# Revit family: Kingsway Sentry Doorset - S_Duralux 405 x 405mm
name_source: partatom
category: Doors
revit_build: Autodesk Revit 2017 (Build: 20160225_1515(x64)
units: mm (PartAtom-declared; Revit-internal decimal feet)

## family parameters
Always vertical = Yes
Cut with Voids When Loaded = No
Host = Wall
OmniClass Number = 23.30.10.00
OmniClass Title = Doors
Room Calculation Point = No
Shared = No

## types (1)
- 1010 x 2100
    Action = Double (Anti-Barricade)
    Analytic Construction = <None>
    Architrave Material = Solid hardwood.
    Bead Material = Stainless steel.
    Configuration = Single Leaf
    Description = In the event of a barricade the SENTRY mechanism
unlocks and folds to allow the door to swing outwards. Equipped with ligature sensors around the three door edges.
    Door - Leaf Finish Notes = Classic Veneer – 'Oak', 'Ash', or 'Beech'
Classic Laminate – 'Formica Door Collection Matte58 Woods', or 'Formica Collection Colors'
Signature - 'Malmo (Egger H877 ST86 Light Lakeland Acacia)', 'Manhattan (Egger H1734 ST9 Intarsie Walnut Horizontal)', or 'Mayfair (Egger H853 ST86 Lava Grey Fleetwood Horizontal)'
    Door Leaf Height = 2054 mm  [stored 6.73885 ft]
    Door Leaf Width = 844 mm
    Durability = Severe Duty Mechanical Strength (DD171).
    Error = No
    Fire Rating = NFR / FD30S
    Frame Thickness = 32 mm  [stored 0.104987 ft]
    Frame Thickness Leading Edge = 44 mm
    Function = Interior
    Height = 2100 mm
    KG280FoldingAntiBarricadeHinge = Yes
    Keynote = L20
    Leaf Core Structure = Flamebreak - Solid timber core comprising three layers of solid hardwood.
    Leaf Height Limits = 2100 mm
    Leaf Swing Radius = 889 mm
    Leaf Width Limits = 1100 mm
    Lipping Material = Exposed 10mm solid hardwood to all four edges.
    Manufacturer = Kingsway Group
    Model = Sentry Doorset
    Rough Height = 2100 mm
    Rough Width = 1010 mm  [stored 3.31365 ft]
    Telephone = 01322 610 470
    Thickness = 54 mm  [stored 0.177165 ft]
    Version = 1.0
    Vision Panel = Duralux Vision Panel (405 mm x 405 mm) with key and thumb turn control.
    Wall Closure = Neither
    Width = 1010 mm  [stored 3.31365 ft]

note: [stored X ft] marks values corroborated as IEEE doubles in the binary element streams (Revit-internal decimal feet)

## geometry (parser evidence)
native form markers: Blend x2, Sweep x37
no freeform markers — native parametric forms only
